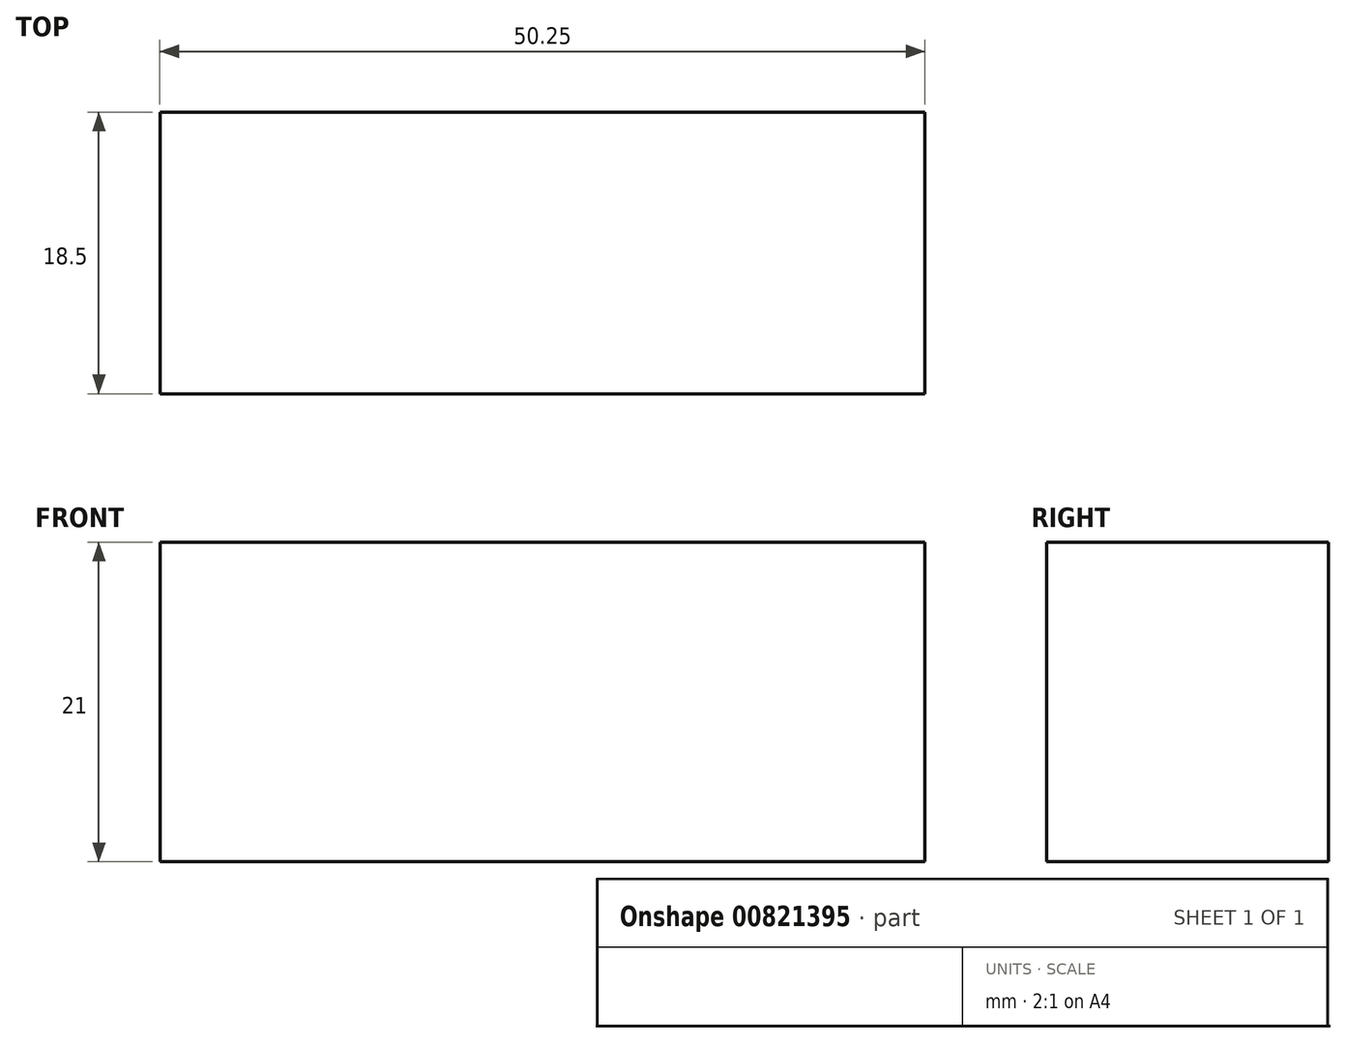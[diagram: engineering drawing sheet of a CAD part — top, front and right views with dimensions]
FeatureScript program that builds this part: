
annotation { "Feature Type Name" : "Feature", "Feature Type Description" : "" }
export const myFeature = defineFeature(function(context is Context, id is Id, definition is map)
    precondition{}
    {
        {
            var Q0;
            Q0=qCreatedBy(makeId("Top.planeOp"),FACE);
            var sketch = newSketch(context, id + "F0", { "sketchPlane" : qUnion([Q0])});
            skLineSegment(sketch, "E0.bottom", {"start": v(0, 0) * mm, "end": v(-50.25, 0) * mm});
            skLineSegment(sketch, "E0.top", {"start": v(0, -18.5) * mm, "end": v(-50.25, -18.5) * mm});
            skLineSegment(sketch, "E0.left", {"start": v(0, 0) * mm, "end": v(0, -18.5) * mm});
            skLineSegment(sketch, "E0.right", {"start": v(-50.25, 0) * mm, "end": v(-50.25, -18.5) * mm});
            skSolve(sketch);
        }
        {
            var Q0;
            Q0 = qSketchRegion(id + "F0", true);
            extrude(context, id + "F1", {"entities" : qUnion([Q0]), "depth" : 21 * mm, "offsetDistance" : 25.4 * mm});
        }
    });
